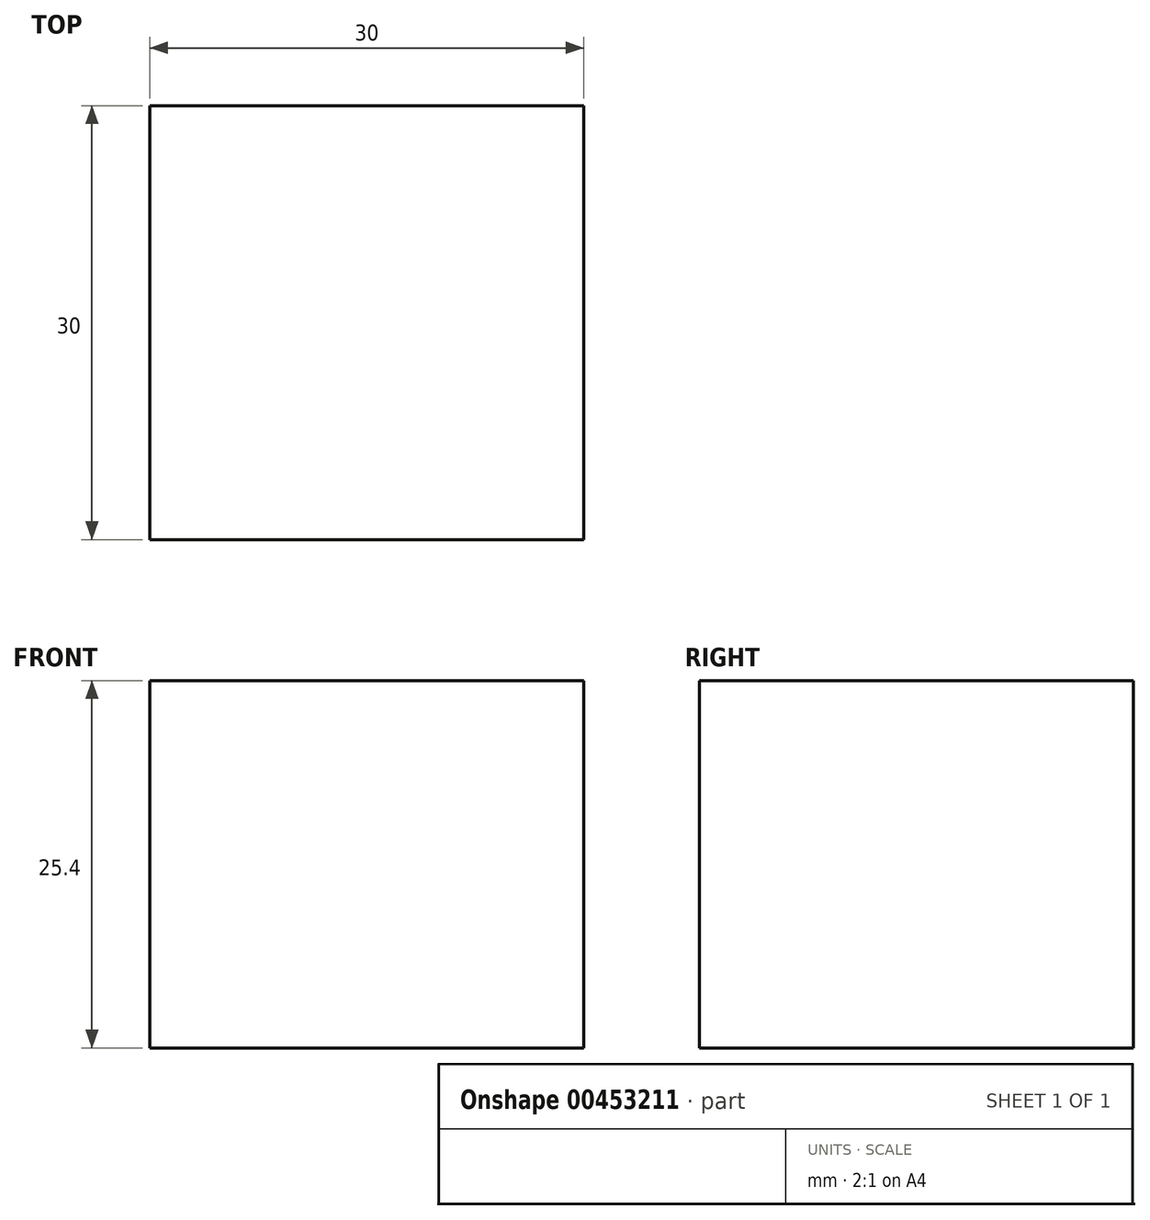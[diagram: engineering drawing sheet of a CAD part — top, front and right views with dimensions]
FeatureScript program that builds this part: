
annotation { "Feature Type Name" : "Feature", "Feature Type Description" : "" }
export const myFeature = defineFeature(function(context is Context, id is Id, definition is map)
    precondition{}
    {
        {
            var Q0;
            Q0=qCreatedBy(makeId("Top.planeOp"),FACE);
            var sketch = newSketch(context, id + "F0", { "sketchPlane" : qUnion([Q0])});
            skLineSegment(sketch, "E0.bottom", {"start": v(-13.96, 21.92) * mm, "end": v(16.04, 21.92) * mm});
            skLineSegment(sketch, "E0.top", {"start": v(-13.96, -8.08) * mm, "end": v(16.04, -8.08) * mm});
            skLineSegment(sketch, "E0.left", {"start": v(-13.96, 21.92) * mm, "end": v(-13.96, -8.08) * mm});
            skLineSegment(sketch, "E0.right", {"start": v(16.04, 21.92) * mm, "end": v(16.04, -8.08) * mm});
            skSolve(sketch);
        }
        {
            var Q0;
            Q0=makeQuery(id+"F0.imprint","IMPRINT",FACE,{"disambiguationData":[TD([[makeQuery(id+"F0.imprint","IMPRINT",EDGE,{"derivedFrom":sQuery(id+"F0.wireOp",EDGE,"E0.bottom")}),-1.0]])]});
            extrude(context, id + "F1", {"entities" : qUnion([Q0]), "depth" : 25.4 * mm});
        }
    });
